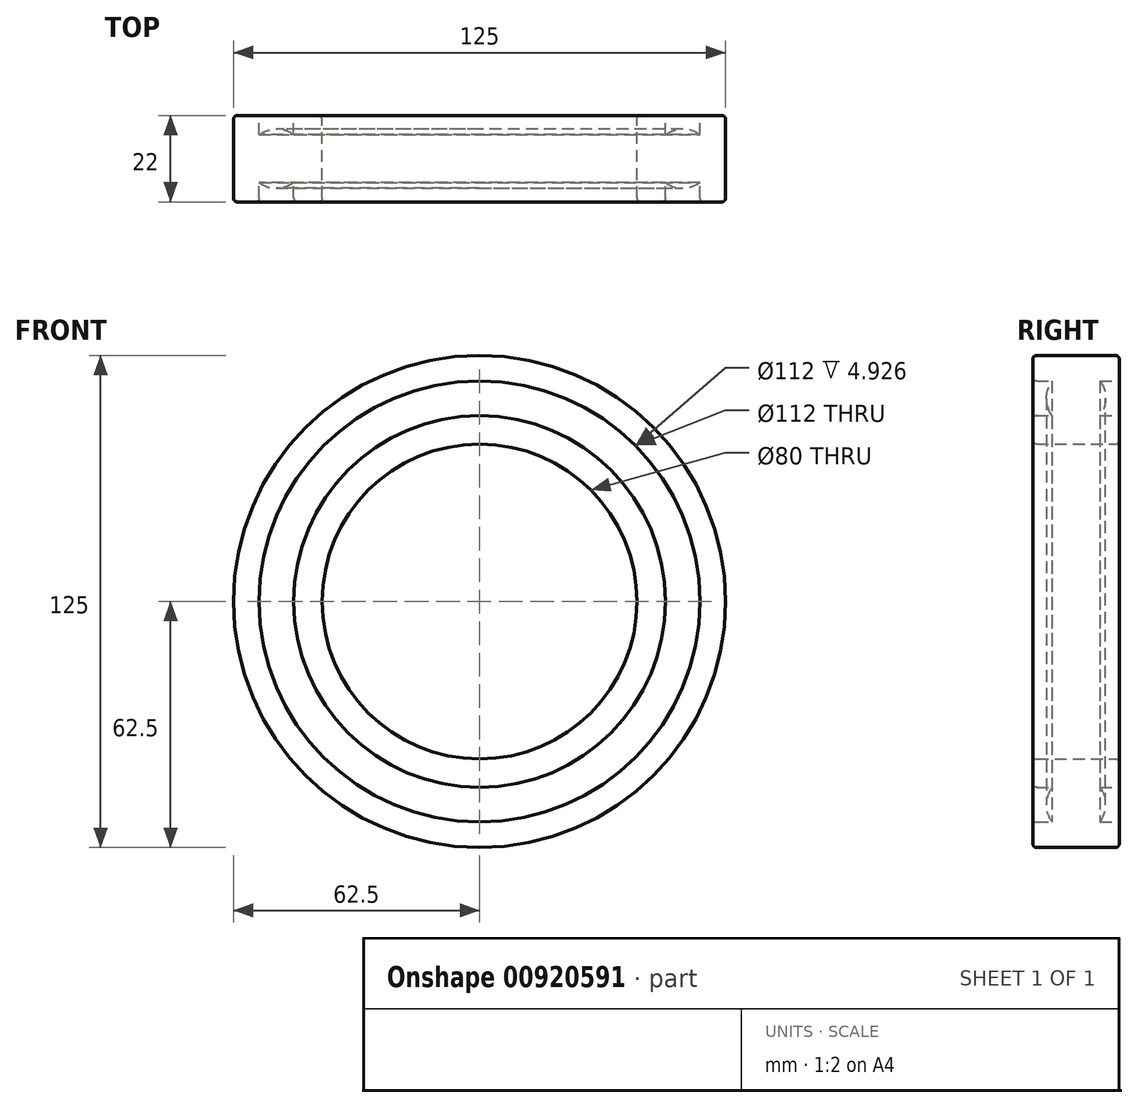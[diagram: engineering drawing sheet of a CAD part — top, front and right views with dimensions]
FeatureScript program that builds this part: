
annotation { "Feature Type Name" : "Feature", "Feature Type Description" : "" }
export const myFeature = defineFeature(function(context is Context, id is Id, definition is map)
    precondition{}
    {
        {
            var Q0;
            Q0=qCreatedBy(makeId("Front.planeOp"),FACE);
            var sketch = newSketch(context, id + "F0", { "sketchPlane" : qUnion([Q0])});
            skCircle(sketch, "E0", {"center": v(0, 0) * mm, "radius": 62.5 * mm});
            skCircle(sketch, "E1", {"center": v(0, 0) * mm, "radius": 40 * mm});
            skSolve(sketch);
        }
        {
            var Q0;
            Q0=makeQuery(id+"F0.imprint","IMPRINT",FACE,{"disambiguationData":[TD([[makeQuery(id+"F0.imprint","IMPRINT",EDGE,{"derivedFrom":sQuery(id+"F0.wireOp",EDGE,"E0")}),1.0]])]});
            extrude(context, id + "F1", {"entities" : qUnion([Q0]), "depth" : 22 * mm, "offsetDistance" : 25 * mm, "symmetric" : true});
        }
        {
            var Q0;
            Q0=qCreatedBy(makeId("Right.planeOp"),FACE);
            var sketch = newSketch(context, id + "F2", { "sketchPlane" : qUnion([Q0])});
            skLineSegment(sketch, "E2", {"start": v(0, 0) * mm, "end": v(32.98, 0) * mm, "construction": true});
            skLineSegment(sketch, "E3.bottom", {"start": v(-21, 56) * mm, "end": v(-6.07, 56) * mm, "construction": true});
            skLineSegment(sketch, "E3.top", {"start": v(-21, 47.2) * mm, "end": v(-6.07, 47.2) * mm, "construction": true});
            skLineSegment(sketch, "E3.left", {"start": v(-21, 56) * mm, "end": v(-21, 47.2) * mm});
            skLineSegment(sketch, "E3.right", {"start": v(21, 56) * mm, "end": v(21, 47.2) * mm});
            skLineSegment(sketch, "E4", {"start": v(0, 55.25) * mm, "end": v(0, 47.95) * mm, "construction": true});
            skLineSegment(sketch, "E5", {"start": v(-6.07, 56) * mm, "end": v(-21, 56) * mm});
            skLineSegment(sketch, "E6", {"start": v(-21, 47.2) * mm, "end": v(-6.07, 47.2) * mm});
            skArc(sketch, "E7", {"start": v(-6.07, 56) * mm, "mid": v(-7.5, 51.6) * mm, "end": v(-6.07, 47.2) * mm});
            skArc(sketch, "E8.trimOffspring", {"start": v(6.07, 47.2) * mm, "mid": v(7.5, 51.6) * mm, "end": v(6.07, 56) * mm});
            skLineSegment(sketch, "E9", {"start": v(6.07, 56) * mm, "end": v(21, 56) * mm});
            skLineSegment(sketch, "E10", {"start": v(6.07, 47.2) * mm, "end": v(21, 47.2) * mm});
            skPoint(sketch, "E11.orphan", {"position": v(21, 54.5) * mm});
            skPoint(sketch, "E12.orphan", {"position": v(21, 48.7) * mm});
            skSolve(sketch);
        }
        {
            var Q0;
            Q0=makeQuery(id+"F2.imprint","IMPRINT",FACE,{"disambiguationData":[TD([[makeQuery(id+"F2.imprint","IMPRINT",EDGE,{"derivedFrom":sQuery(id+"F2.wireOp",EDGE,"E3.left")}),1.0]])]});
            var Q1;
            Q1=makeQuery(id+"F2.imprint","IMPRINT",FACE,{"disambiguationData":[TD([[makeQuery(id+"F2.imprint","IMPRINT",EDGE,{"derivedFrom":sQuery(id+"F2.wireOp",EDGE,"E3.right")}),-1.0]])]});
            var Q2;
            Q2=sQuery(id+"F2.wireOp",EDGE,"E2");
            revolve(context, id + "F3", {"operationType" : NewBodyOperationType.REMOVE, "surfaceOperationType" : NewSurfaceOperationType.NEW, "entities" : qUnion([Q0, Q1]), "axis" : qUnion([Q2]), "revolveType" : RevolveType.FULL, "oppositeDirection" : true});
        }
        {
            var Q0;
            Q0=makeQuery(id+"F1.opExtrude","CAP_EDGE",EDGE,{"disambiguationData":[OSD([sQuery(id+"F0.wireOp",EDGE,"E0")])],"isStart":true});
            var Q1;
            Q1=makeQuery(id+"F1.opExtrude","CAP_EDGE",EDGE,{"disambiguationData":[OSD([sQuery(id+"F0.wireOp",EDGE,"E0")])],"isStart":false});
            var Q2;
            Q2=makeQuery(id+"F1.opExtrude","CAP_EDGE",EDGE,{"disambiguationData":[OSD([sQuery(id+"F0.wireOp",EDGE,"E1")])],"isStart":true});
            var Q3;
            Q3=makeQuery(id+"F1.opExtrude","CAP_EDGE",EDGE,{"disambiguationData":[OSD([sQuery(id+"F0.wireOp",EDGE,"E1")])],"isStart":false});
            var Q4;
            Q4=makeQuery(id+"F3.boolean.opBoolean","INTERSECT",EDGE,{"derivedFrom":[makeQuery(id+"F1.opExtrude","CAP_FACE",FACE,{"disambiguationData":[OSD([sQuery(id+"F0.wireOp",EDGE,"E0"),sQuery(id+"F0.wireOp",EDGE,"E1")])],"isStart":false}),makeQuery(id+"F3.opRevolve","SWEPT_FACE",FACE,{"disambiguationData":[OSD([sQuery(id+"F2.wireOp",EDGE,"E5")])]})]});
            var Q5;
            Q5=makeQuery(id+"F3.boolean.opBoolean","INTERSECT",EDGE,{"derivedFrom":[makeQuery(id+"F1.opExtrude","CAP_FACE",FACE,{"disambiguationData":[OSD([sQuery(id+"F0.wireOp",EDGE,"E0"),sQuery(id+"F0.wireOp",EDGE,"E1")])],"isStart":false}),makeQuery(id+"F3.opRevolve","SWEPT_FACE",FACE,{"disambiguationData":[OSD([sQuery(id+"F2.wireOp",EDGE,"E6")])]})]});
            var Q6;
            Q6=makeQuery(id+"F3.boolean.opBoolean","INTERSECT",EDGE,{"derivedFrom":[makeQuery(id+"F1.opExtrude","CAP_FACE",FACE,{"disambiguationData":[OSD([sQuery(id+"F0.wireOp",EDGE,"E0"),sQuery(id+"F0.wireOp",EDGE,"E1")])],"isStart":true}),makeQuery(id+"F3.opRevolve","SWEPT_FACE",FACE,{"disambiguationData":[OSD([sQuery(id+"F2.wireOp",EDGE,"fW1BCmgC-P2XZ-KUfD-7zd1-HSBjF2vgu6Je")])]})]});
            var Q7;
            Q7=makeQuery(id+"F3.boolean.opBoolean","INTERSECT",EDGE,{"derivedFrom":[makeQuery(id+"F1.opExtrude","CAP_FACE",FACE,{"disambiguationData":[OSD([sQuery(id+"F0.wireOp",EDGE,"E0"),sQuery(id+"F0.wireOp",EDGE,"E1")])],"isStart":true}),makeQuery(id+"F3.opRevolve","SWEPT_FACE",FACE,{"disambiguationData":[OSD([sQuery(id+"F2.wireOp",EDGE,"OryJLgtp-VQlF-1K6k-PiSV-TNUa25SxcoOm")])]})]});
            fillet(context, id + "F4", {"entities" : qUnion([Q0, Q1, Q2, Q3, Q4, Q5, Q6, Q7]), "radius" : 1 * mm, "tangentPropagation" : true, "allowEdgeOverflow" : false});
        }
    });
